# Revit family: Hand_Dryer-Excel_Dryer-XLERATOR_XChanger_Kit
name_source: partatom
category: Specialty Equipment
revit_build: Autodesk Revit 2015 (Build: 20140606_1530(x64)
units: mm (PartAtom-declared; Revit-internal decimal feet)

## types (2) — shared parameters
Body = Metal -  ExcelDryer -Stainless Stainless - #4 Satin Finish
Depth = 0' - 1"
Description = XChanger Kit
Manufacturer = Excel Dryer
Product Documentation Link = http://www.exceldryer.com
Product Name = XLERATOR XChanger Kit
Product Page URL = http://www.exceldryer.com
Product data url = https://bimobject.com
URL = http://www.exceldryer.com
Width = 1' - 5 1/4"

## per-type parameters (varying)
| type | Default Elevation | Height | Model | Void Opening Height | XChanger Kit | XChanger Kit ADA |
| XLERATOR XChanger Kit | 2' - 7 1/16" | 4' - 8 1/8" | # 40575 XLERATOR XChanger Kit | 2' - 6" | Yes | No |
| XLERATOR XChanger Kit ADA | 4' - 0" | 4' - 8" | #40576 XLERATOR XChanger Kit ADA | 1' - 11" | No | Yes |

## geometry (parser evidence)
native form markers: Blend x4, Sweep x2
no freeform markers — native parametric forms only
